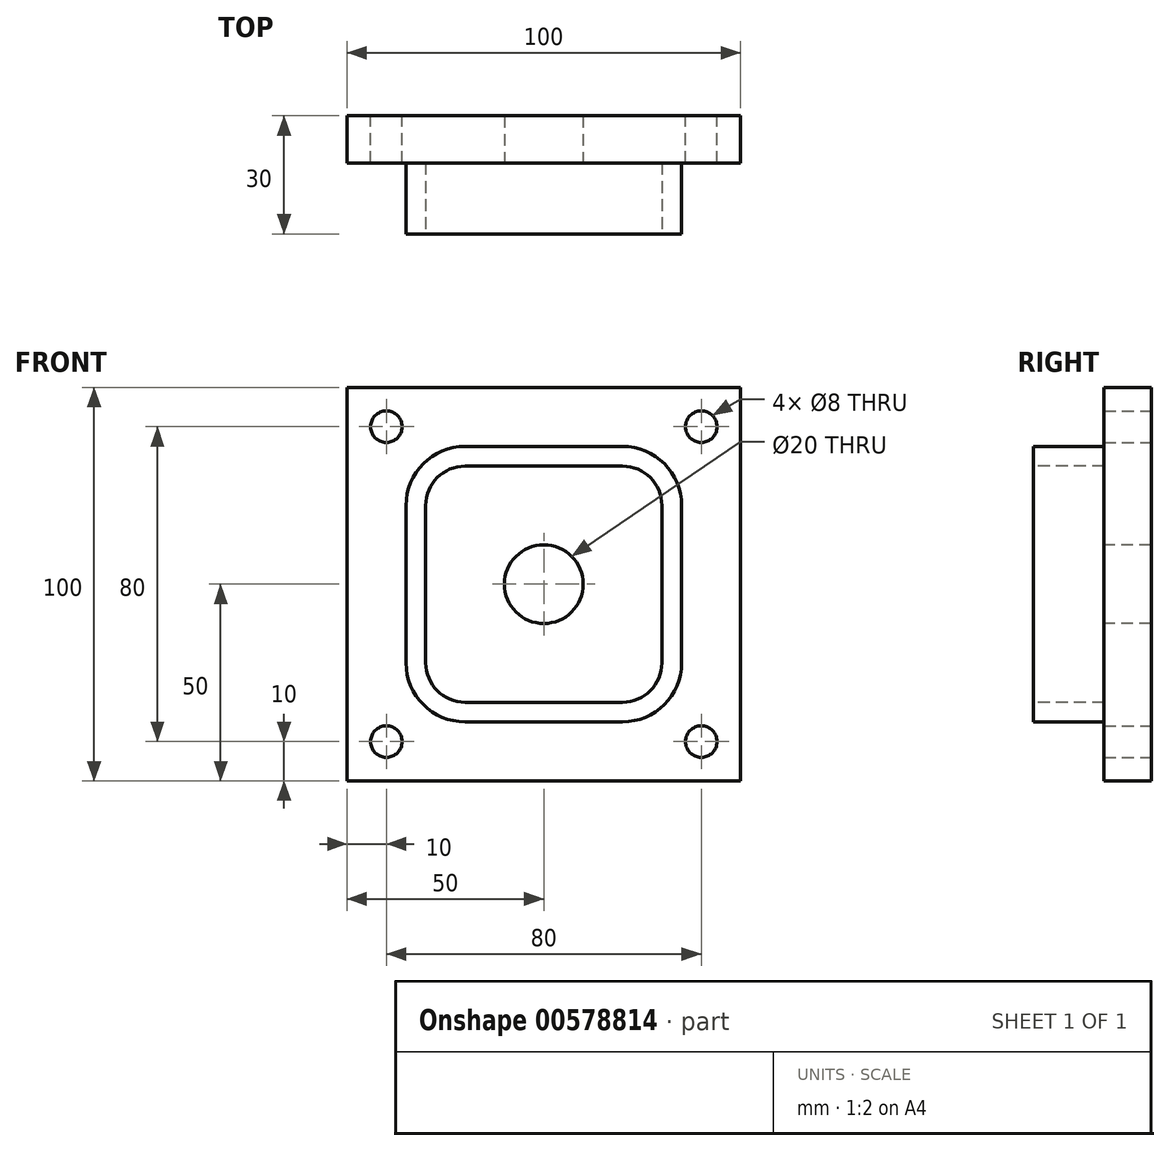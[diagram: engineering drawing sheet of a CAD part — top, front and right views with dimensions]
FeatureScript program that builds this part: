
annotation { "Feature Type Name" : "Feature", "Feature Type Description" : "" }
export const myFeature = defineFeature(function(context is Context, id is Id, definition is map)
    precondition{}
    {
        {
            var Q0;
            Q0=qCreatedBy(makeId("Front.planeOp"),FACE);
            var sketch = newSketch(context, id + "F0", { "sketchPlane" : qUnion([Q0])});
            skLineSegment(sketch, "E0.bottom", {"start": v(-50, 50) * mm, "end": v(50, 50) * mm});
            skLineSegment(sketch, "E0.top", {"start": v(-50, -50) * mm, "end": v(50, -50) * mm});
            skLineSegment(sketch, "E0.left", {"start": v(-50, 50) * mm, "end": v(-50, -50) * mm});
            skLineSegment(sketch, "E0.right", {"start": v(50, 50) * mm, "end": v(50, -50) * mm});
            skPoint(sketch, "E0.middle", {"position": v(0, 0) * mm});
            skCircle(sketch, "E1", {"center": v(-40, 40) * mm, "radius": 4 * mm});
            skCircle(sketch, "E2", {"center": v(-40, -40) * mm, "radius": 4 * mm});
            skCircle(sketch, "E3", {"center": v(40, 40) * mm, "radius": 4 * mm});
            skCircle(sketch, "E4", {"center": v(40, -40) * mm, "radius": 4 * mm});
            skSolve(sketch);
        }
        {
            var Q0;
            Q0=makeQuery(id+"F0.imprint","IMPRINT",FACE,{"disambiguationData":[TD([[makeQuery(id+"F0.imprint","IMPRINT",EDGE,{"derivedFrom":sQuery(id+"F0.wireOp",EDGE,"E0.bottom")}),-1.0]])]});
            extrude(context, id + "F1", {"entities" : qUnion([Q0]), "depth" : 12 * mm, "offsetDistance" : 25 * mm});
        }
        {
            var Q0;
            Q0=makeQuery(id+"F1.opExtrude","CAP_FACE",FACE,{"disambiguationData":[OSD([sQuery(id+"F0.wireOp",EDGE,"E0.bottom"),sQuery(id+"F0.wireOp",EDGE,"E0.top"),sQuery(id+"F0.wireOp",EDGE,"E0.left"),sQuery(id+"F0.wireOp",EDGE,"E0.right"),sQuery(id+"F0.wireOp",EDGE,"E1"),sQuery(id+"F0.wireOp",EDGE,"E2"),sQuery(id+"F0.wireOp",EDGE,"E3"),sQuery(id+"F0.wireOp",EDGE,"E4")])],"isStart":false});
            var sketch = newSketch(context, id + "F2", { "sketchPlane" : qUnion([Q0])});
            skLineSegment(sketch, "E5.bottom", {"start": v(-20, 35) * mm, "end": v(20, 35) * mm});
            skLineSegment(sketch, "E5.top", {"start": v(-20, -35) * mm, "end": v(20, -35) * mm});
            skLineSegment(sketch, "E5.left", {"start": v(-35, 20) * mm, "end": v(-35, -20) * mm});
            skLineSegment(sketch, "E5.right", {"start": v(35, 20) * mm, "end": v(35, -20) * mm});
            skPoint(sketch, "E5.middle", {"position": v(0, 0) * mm});
            skPoint(sketch, "E6.visualSharp", {"position": v(35, 35) * mm});
            skArc(sketch, "E6.filletArc", {"start": v(35, 20) * mm, "mid": v(30.6, 30.6) * mm, "end": v(20, 35) * mm});
            skPoint(sketch, "E7.visualSharp", {"position": v(35, -35) * mm});
            skArc(sketch, "E7.filletArc", {"start": v(20, -35) * mm, "mid": v(30.6, -30.6) * mm, "end": v(35, -20) * mm});
            skPoint(sketch, "E8.visualSharp", {"position": v(-35, 35) * mm});
            skArc(sketch, "E8.filletArc", {"start": v(-20, 35) * mm, "mid": v(-30.6, 30.6) * mm, "end": v(-35, 20) * mm});
            skPoint(sketch, "E9.visualSharp", {"position": v(-35, -35) * mm});
            skArc(sketch, "E9.filletArc", {"start": v(-35, -20) * mm, "mid": v(-30.6, -30.6) * mm, "end": v(-20, -35) * mm});
            skSolve(sketch);
        }
        {
            var Q0;
            Q0=makeQuery(id+"F2.imprint","IMPRINT",FACE,{"disambiguationData":[TD([[makeQuery(id+"F2.imprint","IMPRINT",EDGE,{"derivedFrom":sQuery(id+"F2.wireOp",EDGE,"E5.bottom")}),-1.0]])]});
            extrude(context, id + "F3", {"entities" : qUnion([Q0]), "operationType" : NewBodyOperationType.ADD, "depth" : 18 * mm, "offsetDistance" : 25 * mm});
        }
        {
            var Q0;
            Q0=makeQuery(id+"F3.opExtrude","CAP_FACE",FACE,{"disambiguationData":[OSD([sQuery(id+"F2.wireOp",EDGE,"E5.bottom"),sQuery(id+"F2.wireOp",EDGE,"E5.top"),sQuery(id+"F2.wireOp",EDGE,"E5.left"),sQuery(id+"F2.wireOp",EDGE,"E5.right"),sQuery(id+"F2.wireOp",EDGE,"E6.filletArc"),sQuery(id+"F2.wireOp",EDGE,"E7.filletArc"),sQuery(id+"F2.wireOp",EDGE,"E8.filletArc"),sQuery(id+"F2.wireOp",EDGE,"E9.filletArc")])],"isStart":false});
            var sketch = newSketch(context, id + "F4", { "sketchPlane" : qUnion([Q0])});
            skLineSegment(sketch, "E10.bottom", {"start": v(-20, 30) * mm, "end": v(20, 30) * mm});
            skLineSegment(sketch, "E10.top", {"start": v(-20, -30) * mm, "end": v(20, -30) * mm});
            skLineSegment(sketch, "E10.left", {"start": v(-30, 20) * mm, "end": v(-30, -20) * mm});
            skLineSegment(sketch, "E10.right", {"start": v(30, 20) * mm, "end": v(30, -20) * mm});
            skPoint(sketch, "E10.middle", {"position": v(0, 0) * mm});
            skPoint(sketch, "E11.visualSharp", {"position": v(30, 30) * mm});
            skArc(sketch, "E11.filletArc", {"start": v(30, 20) * mm, "mid": v(27.07, 27.07) * mm, "end": v(20, 30) * mm});
            skPoint(sketch, "E12.visualSharp", {"position": v(30, -30) * mm});
            skArc(sketch, "E12.filletArc", {"start": v(20, -30) * mm, "mid": v(27.07, -27.07) * mm, "end": v(30, -20) * mm});
            skPoint(sketch, "E13.visualSharp", {"position": v(-30, 30) * mm});
            skArc(sketch, "E13.filletArc", {"start": v(-20, 30) * mm, "mid": v(-27.07, 27.07) * mm, "end": v(-30, 20) * mm});
            skPoint(sketch, "E14.visualSharp", {"position": v(-30, -30) * mm});
            skArc(sketch, "E14.filletArc", {"start": v(-30, -20) * mm, "mid": v(-27.07, -27.07) * mm, "end": v(-20, -30) * mm});
            skSolve(sketch);
        }
        {
            var Q0;
            Q0=makeQuery(id+"F4.imprint","IMPRINT",FACE,{"disambiguationData":[TD([[makeQuery(id+"F4.imprint","IMPRINT",EDGE,{"derivedFrom":sQuery(id+"F4.wireOp",EDGE,"E10.bottom")}),-1.0]])]});
            extrude(context, id + "F5", {"entities" : qUnion([Q0]), "operationType" : NewBodyOperationType.REMOVE, "oppositeDirection" : true, "depth" : 18 * mm, "offsetDistance" : 25 * mm});
        }
        {
            var Q0;
            Q0=makeQuery(id+"F5.boolean.opBoolean","COPY",FACE,{"derivedFrom":makeQuery(id+"F5.opExtrude","CAP_FACE",FACE,{"disambiguationData":[OSD([sQuery(id+"F4.wireOp",EDGE,"E10.bottom"),sQuery(id+"F4.wireOp",EDGE,"E10.top"),sQuery(id+"F4.wireOp",EDGE,"E10.left"),sQuery(id+"F4.wireOp",EDGE,"E10.right"),sQuery(id+"F4.wireOp",EDGE,"E11.filletArc"),sQuery(id+"F4.wireOp",EDGE,"E12.filletArc"),sQuery(id+"F4.wireOp",EDGE,"E13.filletArc"),sQuery(id+"F4.wireOp",EDGE,"E14.filletArc")])],"isStart":false})});
            var sketch = newSketch(context, id + "F6", { "sketchPlane" : qUnion([Q0])});
            skCircle(sketch, "E15", {"center": v(0, 0) * mm, "radius": 10 * mm});
            skSolve(sketch);
        }
        {
            var Q0;
            Q0=makeQuery(id+"F6.imprint","IMPRINT",FACE,{"disambiguationData":[TD([[makeQuery(id+"F6.imprint","IMPRINT",EDGE,{"derivedFrom":sQuery(id+"F6.wireOp",EDGE,"E15")}),1.0]])]});
            extrude(context, id + "F7", {"entities" : qUnion([Q0]), "operationType" : NewBodyOperationType.REMOVE, "oppositeDirection" : true, "depth" : 30 * mm, "offsetDistance" : 25 * mm});
        }
    });
